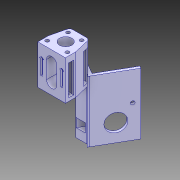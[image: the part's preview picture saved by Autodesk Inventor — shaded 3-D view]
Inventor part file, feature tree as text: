
AUTODESK INVENTOR PART (.ipt)
format: ipt  version: 2018 (Build 220112000, 112)  size: 493,568 bytes
history: native  units: mm
features: other x16, extrude x10, sketch x9
ambient origin geometry x8: Origin, YZ Plane, XZ Plane, XY Plane, X Axis, Y Axis, Z Axis, Center Point
bodies: Body1 (feature_tree)
feature tree (35):
  other  "Sólido1"
  extrude  "Extrusión1"  Depth=3.0mm
  other  "Edición directa3"
  other  "Edición directa4"
  extrude  "Extrusión2"  Depth=3.0mm
  extrude  "Extrusión3"  TaperAngle=0.0deg  [1 undecoded]
  extrude  "Extrusión7"  TaperAngle=0.0deg  [1 undecoded]
  other  "Edición directa8"
  other  "Edición directa11"
  extrude  "Extrusión14"  Depth=7.0mm
  extrude  "Extrusión15"  Depth=7.0mm
  extrude  "Extrusión16"  Depth=7.0mm
  extrude  "Extrusión17"  Depth=1.0mm
  other  "Edición directa12"
  extrude  "Extrusión18"  Depth=4.0mm
  extrude  "Extrusión19"  Depth=3.0mm
  other  "Edición directa13"
  sketch  "Boceto1"  dims[d6=3.0mm d7=3.0mm]
  sketch  "Boceto2"  dims[d8=3.0mm d9=3.0mm]
  sketch  "Boceto4"  dims[d10=3.0mm d11=0.0mm d15=0.0mm d16=0.0mm d17=-2.5mm]
  sketch  "Boceto16"  dims[d18=0.0mm d19=0.0mm d20=-2.5mm d21=0.0mm d22=0.0mm d23=-1.5mm]
  sketch  "Boceto17"  dims[d24=0.0mm d25=0.0mm d26=-2.0mm d27=7.0mm]
  sketch  "Boceto18"  dims[d28=7.0mm d29=7.0mm]
  sketch  "Boceto19"  dims[d30=7.0mm d31=7.0mm]
  sketch  "Boceto20"  dims[d32=0.0mm d33=1.0mm]
  sketch  "Boceto21"  dims[d34=1.0mm d35=4.0mm d36=3.0mm d37=1.5mm d39=1.5mm d40=1.5mm d41=0.0mm d59=3.0mm d62=55.0mm d63=0.0mm d97=0.0mm d98=0.0mm d99=10.0mm d108=0.0mm d109=0.0mm d110=10.0mm d111=15.0mm d112=90.0deg d113=15.0mm d114=9.5mm d115=0.0mm d120=4.2mm d121=4.2mm d123=10.0mm d126=10.0mm d127=11.0mm d128=0.0mm d129=10.0mm d130=50.0mm d131=120.0deg d132=40.0mm d133=120.0deg d134=3.0mm d135=40.0mm d136=15.0mm d137=3.0mm d138=55.0mm d139=0.0mm d140=10.0mm d141=0.0mm d142=0.0mm d143=0.0mm d144=3.0mm d145=38.0mm d146=32.0mm d147=24.0mm d148=15.0mm d150=4.0mm d151=3.0mm d152=0.0mm d153=20.0mm d154=3.0mm d156=10.0mm d157=10.0mm d158=0.0mm d159=0.0mm d160=0.0mm d161=5.0mm]
  other  "PartBody"
  other  "Desplazar4"
  other  "Desplazar5"
  other  "Desplazar6"
  other  "Desplazar7"
  other  "Desplazar13"
  other  "Desplazar16"
  other  "Desplazar17"
  other  "Desplazar18"
note: 2 required parameter values undecoded (feature->parameter linkage not recoverable at this tier; creation-order binding heuristic only, values carry confidence <= 0.55)
